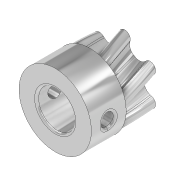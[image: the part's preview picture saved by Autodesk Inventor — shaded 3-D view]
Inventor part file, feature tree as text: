
AUTODESK INVENTOR PART (.ipt)
format: ipt  version: 2020 (Build 240168000, 168)  size: 576,000 bytes
history: native  units: in
note: dims shown in document units (in); Inventor stores cm internally (conversion verified against a paired STEP export)
features: sketch x7, sweep x2, extrude x2, fillet x2, projected_geometry x2, chamfer x1, other x1
ambient origin geometry x8: Origin, YZ Plane, XZ Plane, XY Plane, X Axis, Y Axis, Z Axis, Center Point
bodies: Solid1 (feature_tree)
feature tree (17):
  sweep  "Sweep1"
  sketch  "3D Sketch2"
  extrude  "Extrusion1"  Depth=0.0787in
  extrude  "Extrusion2"  Depth=0.0787in
  fillet  "Fillet1"  Radius=2.3622in
  sweep  "Sweep2"
  chamfer  "Chamfer1"  Distance=0.1969in
  fillet  "Fillet2"  Radius=0.0748in
  sketch  "Sketch1"  dims[d0=0.1969in d1=0.4094in]
  sketch  "3D Sketch1"
  other  "Helical Curve1"
  sketch  "Sketch2"  dims[d2=0.0866in d3=0.0787in]
  projected_geometry  "Projected Loop1"
  sketch  "Sketch3"  dims[d4=0.0787in d5=0.0787in d6=2.3622in d8=360.0deg]
  sketch  "Sketch4"  dims[d10=0.1969in d11=0.0236in d12=0.236in d13=0.0in d14=0.0in d15=0.0in d16=0.1969in d17=0.0in d18=0.0748in d19=0.205in d20=0.0in d21=0.0118in d22=0.0079in d23=0.0in d24=0.0in d25=0.1969in d26=0.125in d27=0.0137in d28=0.0118in]
  projected_geometry  "Projected Loop2"
  sketch  "3D Sketch3"
